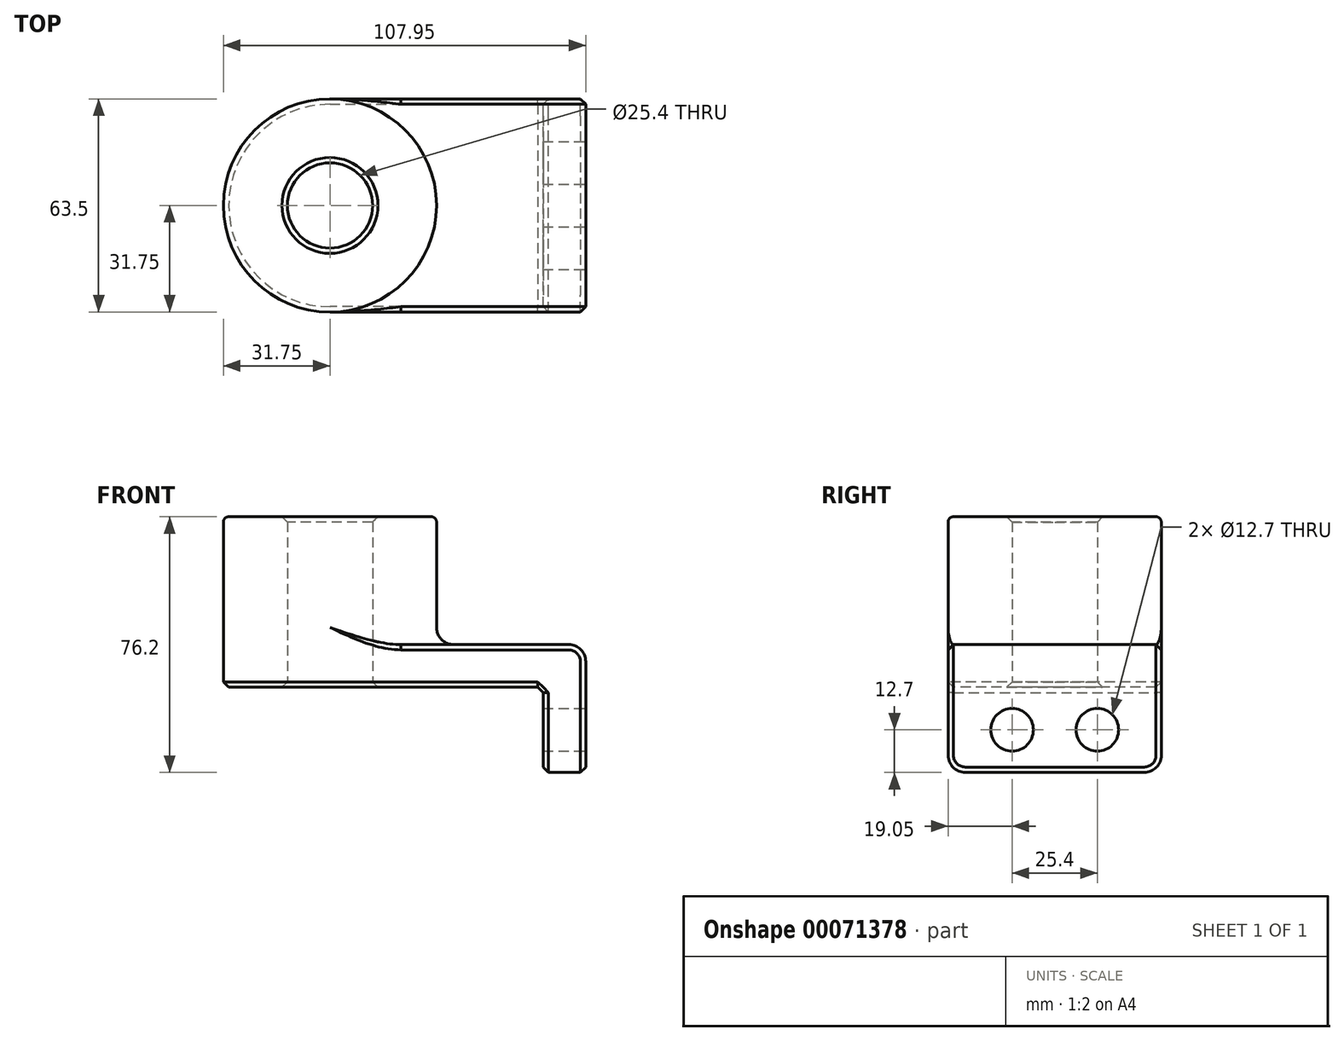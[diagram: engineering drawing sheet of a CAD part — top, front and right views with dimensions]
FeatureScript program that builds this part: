
annotation { "Feature Type Name" : "Feature", "Feature Type Description" : "" }
export const myFeature = defineFeature(function(context is Context, id is Id, definition is map)
    precondition{}
    {
        {
            var Q0;
            Q0=qCreatedBy(makeId("Top.planeOp"),FACE);
            var sketch = newSketch(context, id + "F0", { "sketchPlane" : qUnion([Q0])});
            skLineSegment(sketch, "E0.rect.bottom", {"start": v(38.1, 31.75) * mm, "end": v(-38.1, 31.75) * mm});
            skLineSegment(sketch, "E0.rect.top", {"start": v(38.1, -31.75) * mm, "end": v(-38.1, -31.75) * mm});
            skLineSegment(sketch, "E0.rect.left", {"start": v(38.1, 31.75) * mm, "end": v(38.1, -31.75) * mm});
            skLineSegment(sketch, "E0.rect.right", {"start": v(-38.1, 31.75) * mm, "end": v(-38.1, -31.75) * mm});
            skPoint(sketch, "E0.rect.middle", {"position": v(0, 0) * mm});
            skCircle(sketch, "E1", {"center": v(-38.1, 0) * mm, "radius": 31.75 * mm});
            skCircle(sketch, "E2", {"center": v(-38.1, 0) * mm, "radius": 12.7 * mm});
            skSolve(sketch);
        }
        {
            var Q0;
            Q0 = qSketchRegion(id + "F0", true);
            extrude(context, id + "F1", {"entities" : qUnion([Q0]), "depth" : 12.7 * mm});
        }
        {
            var Q0;
            {var subQ1=sQuery(id+"F0.wireOp",EDGE,"E0.rect.right");var subQ3=sQuery(id+"F0.wireOp",EDGE,"E2");var subQ4=makeQuery(id+"F0.imprint","INTERSECT",VERTEX,{"disambiguationData":[OD(0.0)],"derivedFrom":[subQ1,subQ3]});Q0=makeQuery(id+"F0.imprint","IMPRINT",FACE,{"disambiguationData":[TD([[makeQuery(id+"F0.imprint","IMPRINT",EDGE,{"disambiguationData":[TD([[subQ4,-1.0]])],"derivedFrom":subQ3}),-1.0]])]});}
            var Q1;
            {var subQ1=sQuery(id+"F0.wireOp",EDGE,"E0.rect.right");var subQ3=sQuery(id+"F0.wireOp",EDGE,"E2");var subQ4=makeQuery(id+"F0.imprint","INTERSECT",VERTEX,{"disambiguationData":[OD(0.0)],"derivedFrom":[subQ1,subQ3]});Q1=makeQuery(id+"F0.imprint","IMPRINT",FACE,{"disambiguationData":[TD([[makeQuery(id+"F0.imprint","IMPRINT",EDGE,{"disambiguationData":[TD([[subQ4,1.0]])],"derivedFrom":subQ3}),-1.0]])]});}
            extrude(context, id + "F2", {"entities" : qUnion([Q0, Q1]), "operationType" : NewBodyOperationType.ADD, "depth" : 50.8 * mm});
        }
        {
            var Q0;
            Q0=makeQuery(id+"F1.opExtrude","SWEPT_FACE",FACE,{"disambiguationData":[OSD([sQuery(id+"F0.wireOp",EDGE,"E0.rect.left")])]});
            var sketch = newSketch(context, id + "F3", { "sketchPlane" : qUnion([Q0])});
            skLineSegment(sketch, "E3.bottom", {"start": v(-31.75, 12.7) * mm, "end": v(31.75, 12.7) * mm});
            skLineSegment(sketch, "E3.top", {"start": v(-31.75, -25.4) * mm, "end": v(31.75, -25.4) * mm});
            skLineSegment(sketch, "E3.left", {"start": v(-31.75, 12.7) * mm, "end": v(-31.75, -25.4) * mm});
            skLineSegment(sketch, "E3.right", {"start": v(31.75, 12.7) * mm, "end": v(31.75, -25.4) * mm});
            skLineSegment(sketch, "E4", {"start": v(0, 0) * mm, "end": v(0, -25.4) * mm});
            skCircle(sketch, "E5", {"center": v(-12.7, -12.7) * mm, "radius": 6.35 * mm});
            skCircle(sketch, "E6.MirrorC", {"center": v(12.7, -12.7) * mm, "radius": 6.35 * mm});
            skSolve(sketch);
        }
        {
            var Q0;
            {var subQ5=sQuery(id+"F3.wireOp",EDGE,"E4");Q0=makeQuery(id+"F3.imprint","IMPRINT",FACE,{"disambiguationData":[TD([[makeQuery(id+"F3.imprint","IMPRINT",EDGE,{"derivedFrom":subQ5}),-1.0]])]});}
            var Q1;
            {var subQ0=sQuery(id+"F3.wireOp",EDGE,"E4");Q1=makeQuery(id+"F3.imprint","IMPRINT",FACE,{"disambiguationData":[TD([[makeQuery(id+"F3.imprint","IMPRINT",EDGE,{"derivedFrom":subQ0}),1.0]])]});}
            var Q2;
            {var subQ4=sQuery(id+"F3.wireOp",EDGE,"E3.bottom");Q2=makeQuery(id+"F3.imprint","IMPRINT",FACE,{"disambiguationData":[TD([[makeQuery(id+"F3.imprint","IMPRINT",EDGE,{"derivedFrom":subQ4}),1.0]])]});}
            extrude(context, id + "F4", {"entities" : qUnion([Q0, Q1, Q2]), "operationType" : NewBodyOperationType.ADD, "oppositeDirection" : true, "depth" : 12.7 * mm});
        }
        {
            var Q0;
            {var subQ0=sQuery(id+"F0.wireOp",EDGE,"E1");Q0=makeQuery(id+"F2.boolean.opBoolean","INTERSECT",EDGE,{"derivedFrom":[makeQuery(id+"F1.opExtrude","CAP_FACE",FACE,{"disambiguationData":[OSD([sQuery(id+"F0.wireOp",EDGE,"E0.rect.bottom"),sQuery(id+"F0.wireOp",EDGE,"E0.rect.top"),sQuery(id+"F0.wireOp",EDGE,"E0.rect.left"),subQ0,sQuery(id+"F0.wireOp",EDGE,"E2")])],"isStart":false}),makeQuery(id+"F2.opExtrude","SWEPT_FACE",FACE,{"disambiguationData":[OSD([subQ0])]})]});}
            var Q1;
            Q1=makeQuery(id+"F1.opExtrude","CAP_EDGE",EDGE,{"disambiguationData":[OSD([sQuery(id+"F0.wireOp",EDGE,"E0.rect.left")])],"isStart":false});
            var Q2;
            Q2=makeQuery(id+"F4.opExtrude","SWEPT_EDGE",EDGE,{"disambiguationData":[OSD([sQuery(id+"F3.wireOp",EDGE,"E3.top"),sQuery(id+"F3.wireOp",EDGE,"E3.left")])]});
            var Q3;
            Q3=makeQuery(id+"F4.opExtrude","SWEPT_EDGE",EDGE,{"disambiguationData":[OSD([sQuery(id+"F3.wireOp",EDGE,"E3.top"),sQuery(id+"F3.wireOp",EDGE,"E3.right")])]});
            fillet(context, id + "F5", {"entities" : qUnion([Q0, Q1, Q2, Q3]), "radius" : 5.08 * mm, "tangentPropagation" : true, "allowEdgeOverflow" : false});
        }
        {
            var Q0;
            Q0=makeQuery(id+"F1.opExtrude","CAP_EDGE",EDGE,{"disambiguationData":[OSD([sQuery(id+"F0.wireOp",EDGE,"E0.rect.bottom")])],"isStart":false});
            var Q1;
            Q1=makeQuery(id+"F1.opExtrude","CAP_EDGE",EDGE,{"disambiguationData":[OSD([sQuery(id+"F0.wireOp",EDGE,"E0.rect.bottom")])],"isStart":true});
            var Q2;
            Q2=makeQuery(id+"F4.boolean.opBoolean","INTERSECT",EDGE,{"derivedFrom":[makeQuery(id+"F1.opExtrude","CAP_FACE",FACE,{"disambiguationData":[OSD([sQuery(id+"F0.wireOp",EDGE,"E0.rect.bottom"),sQuery(id+"F0.wireOp",EDGE,"E0.rect.top"),sQuery(id+"F0.wireOp",EDGE,"E0.rect.left"),sQuery(id+"F0.wireOp",EDGE,"E1"),sQuery(id+"F0.wireOp",EDGE,"E2")])],"isStart":true}),makeQuery(id+"F4.opExtrude","CAP_FACE",FACE,{"disambiguationData":[OSD([sQuery(id+"F3.wireOp",EDGE,"E3.bottom"),sQuery(id+"F3.wireOp",EDGE,"E3.top"),sQuery(id+"F3.wireOp",EDGE,"E3.left"),sQuery(id+"F3.wireOp",EDGE,"E3.right"),sQuery(id+"F3.wireOp",EDGE,"E5"),sQuery(id+"F3.wireOp",EDGE,"E6.MirrorC")])],"isStart":false})]});
            var Q3;
            Q3=makeQuery(id+"F1.opExtrude","CAP_EDGE",EDGE,{"disambiguationData":[OSD([sQuery(id+"F0.wireOp",EDGE,"E0.rect.top")])],"isStart":false});
            var Q4;
            Q4=makeQuery(id+"F1.opExtrude","CAP_EDGE",EDGE,{"disambiguationData":[OSD([sQuery(id+"F0.wireOp",EDGE,"E0.rect.top")])],"isStart":true});
            chamfer(context, id + "F6", {"entities" : qUnion([Q0, Q1, Q2, Q3, Q4]), "width" : 1.59 * mm, "tangentPropagation" : true});
        }
        {
            var Q0;
            {var subQ0=sQuery(id+"F0.wireOp",EDGE,"E2");Q0=makeQuery(id+"F2.boolean.opBoolean","MERGE",FACE,{"derivedFrom":[makeQuery(id+"F1.opExtrude","SWEPT_FACE",FACE,{"disambiguationData":[OSD([subQ0])]}),makeQuery(id+"F2.opExtrude","SWEPT_FACE",FACE,{"disambiguationData":[OSD([subQ0])]})]});}
            chamfer(context, id + "F7", {"entities" : qUnion([Q0]), "width" : 1.59 * mm, "tangentPropagation" : true});
        }
        {
            var Q0;
            Q0=makeQuery(id+"F2.opExtrude","CAP_EDGE",EDGE,{"disambiguationData":[OSD([sQuery(id+"F0.wireOp",EDGE,"E1")])],"isStart":false});
            fillet(context, id + "F8", {"entities" : qUnion([Q0]), "radius" : 1.59 * mm, "tangentPropagation" : true, "allowEdgeOverflow" : false});
        }
    });
